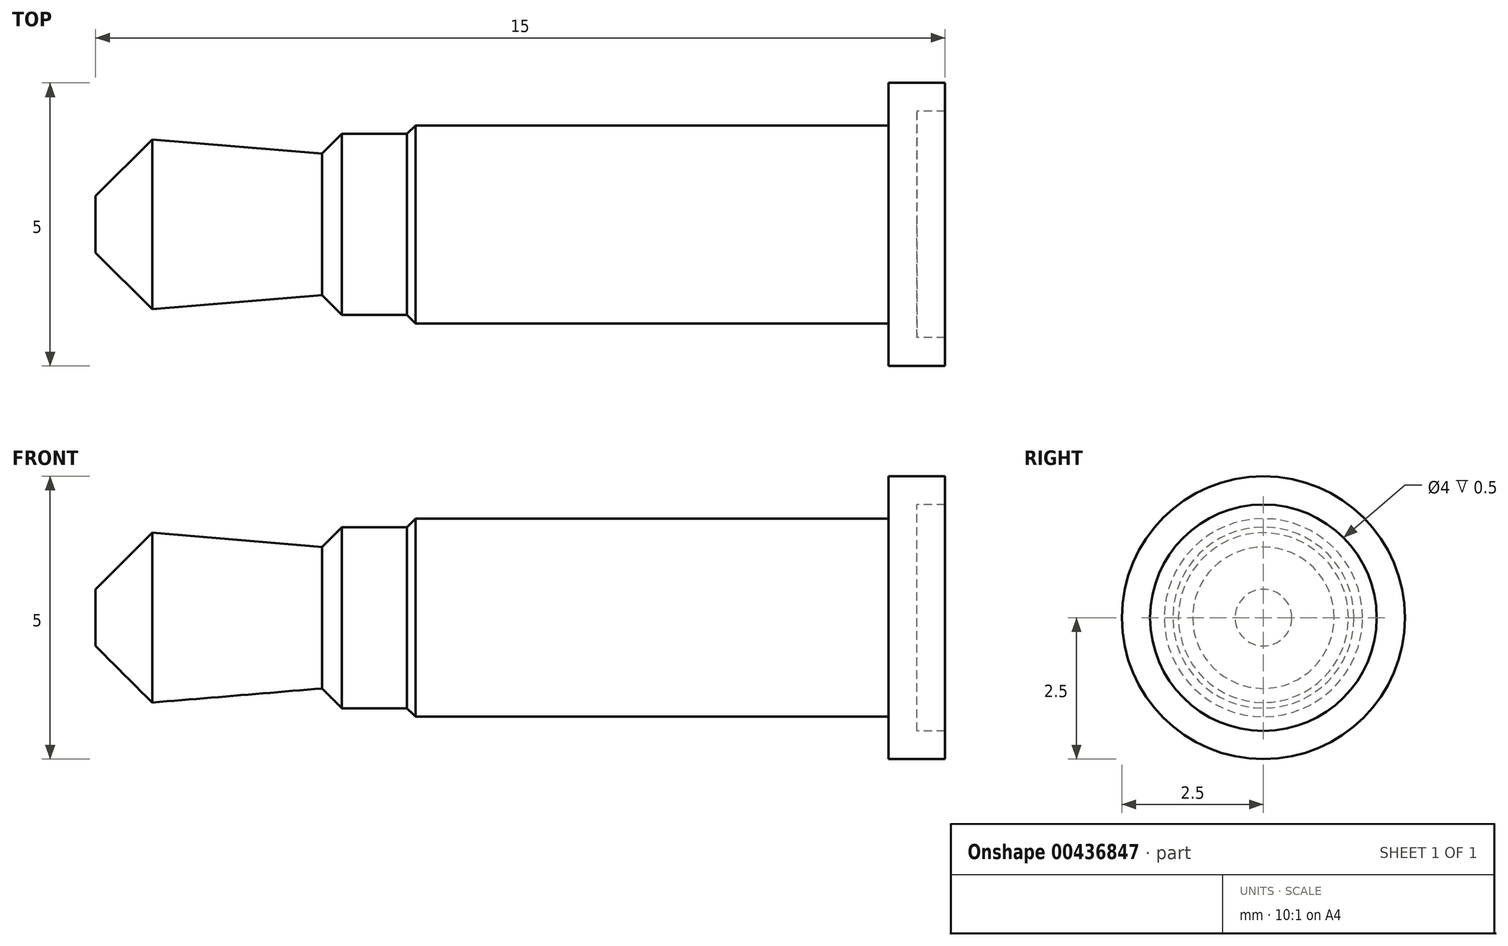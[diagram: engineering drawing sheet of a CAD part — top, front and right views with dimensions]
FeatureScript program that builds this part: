
annotation { "Feature Type Name" : "Feature", "Feature Type Description" : "" }
export const myFeature = defineFeature(function(context is Context, id is Id, definition is map)
    precondition{}
    {
        {
            var Q0;
            Q0=qCreatedBy(makeId("Front.planeOp"),FACE);
            var sketch = newSketch(context, id + "F0", { "sketchPlane" : qUnion([Q0])});
            skLineSegment(sketch, "E0", {"start": v(0, 0) * mm, "end": v(0, 0.5) * mm});
            skLineSegment(sketch, "E1", {"start": v(0, 0.5) * mm, "end": v(1, 1.5) * mm});
            skLineSegment(sketch, "E2", {"start": v(1, 1.5) * mm, "end": v(4, 1.25) * mm});
            skLineSegment(sketch, "E3", {"start": v(4, 1.25) * mm, "end": v(4.35, 1.6) * mm});
            skLineSegment(sketch, "E4", {"start": v(4.35, 1.6) * mm, "end": v(5.5, 1.6) * mm});
            skLineSegment(sketch, "E5", {"start": v(5.5, 1.6) * mm, "end": v(5.65, 1.75) * mm});
            skLineSegment(sketch, "E6", {"start": v(5.65, 1.75) * mm, "end": v(14, 1.75) * mm});
            skLineSegment(sketch, "E7", {"start": v(14, 1.75) * mm, "end": v(14, 2.5) * mm});
            skLineSegment(sketch, "E8", {"start": v(14, 2.5) * mm, "end": v(15, 2.5) * mm});
            skLineSegment(sketch, "E9", {"start": v(15, 2.5) * mm, "end": v(15, 0) * mm});
            skLineSegment(sketch, "E10", {"start": v(15, 0) * mm, "end": v(0, 0) * mm});
            skSolve(sketch);
        }
        {
            var Q0;
            Q0=makeQuery(id+"F0.imprint","IMPRINT",FACE,{"disambiguationData":[TD([[makeQuery(id+"F0.imprint","IMPRINT",EDGE,{"derivedFrom":sQuery(id+"F0.wireOp",EDGE,"E0")}),-1.0]])]});
            var Q1;
            Q1=sQuery(id+"F0.wireOp",EDGE,"E10");
            revolve(context, id + "F1", {"entities" : qUnion([Q0]), "axis" : qUnion([Q1]), "revolveType" : RevolveType.FULL});
        }
        {
            var Q0;
            Q0=makeQuery(id+"F1.opRevolve","SWEPT_FACE",FACE,{"disambiguationData":[OSD([sQuery(id+"F0.wireOp",EDGE,"E9")])]});
            var sketch = newSketch(context, id + "F2", { "sketchPlane" : qUnion([Q0])});
            skCircle(sketch, "E11", {"center": v(0, 0) * mm, "radius": 2 * mm});
            skSolve(sketch);
        }
        {
            var Q0;
            Q0 = qSketchRegion(id + "F2", true);
            extrude(context, id + "F3", {"entities" : qUnion([Q0]), "operationType" : NewBodyOperationType.REMOVE, "oppositeDirection" : true, "depth" : 0.5 * mm});
        }
        {
            var Q0;
            Q0=makeQuery(id+"F3.boolean.opBoolean","COPY",FACE,{"derivedFrom":makeQuery(id+"F3.opExtrude","CAP_FACE",FACE,{"disambiguationData":[OSD([sQuery(id+"F2.wireOp",EDGE,"E11")])],"isStart":false})});
            var sketch = newSketch(context, id + "F4", { "sketchPlane" : qUnion([Q0])});
            skCircle(sketch, "E12.0", {"center": v(0, 0) * mm, "radius": 2 * mm});
            skSolve(sketch);
        }
        {
            var Q0;
            Q0 = qSketchRegion(id + "F4", true);
            extrude(context, id + "F5", {"entities" : qUnion([Q0]), "depth" : 0.5 * mm});
        }
    });
